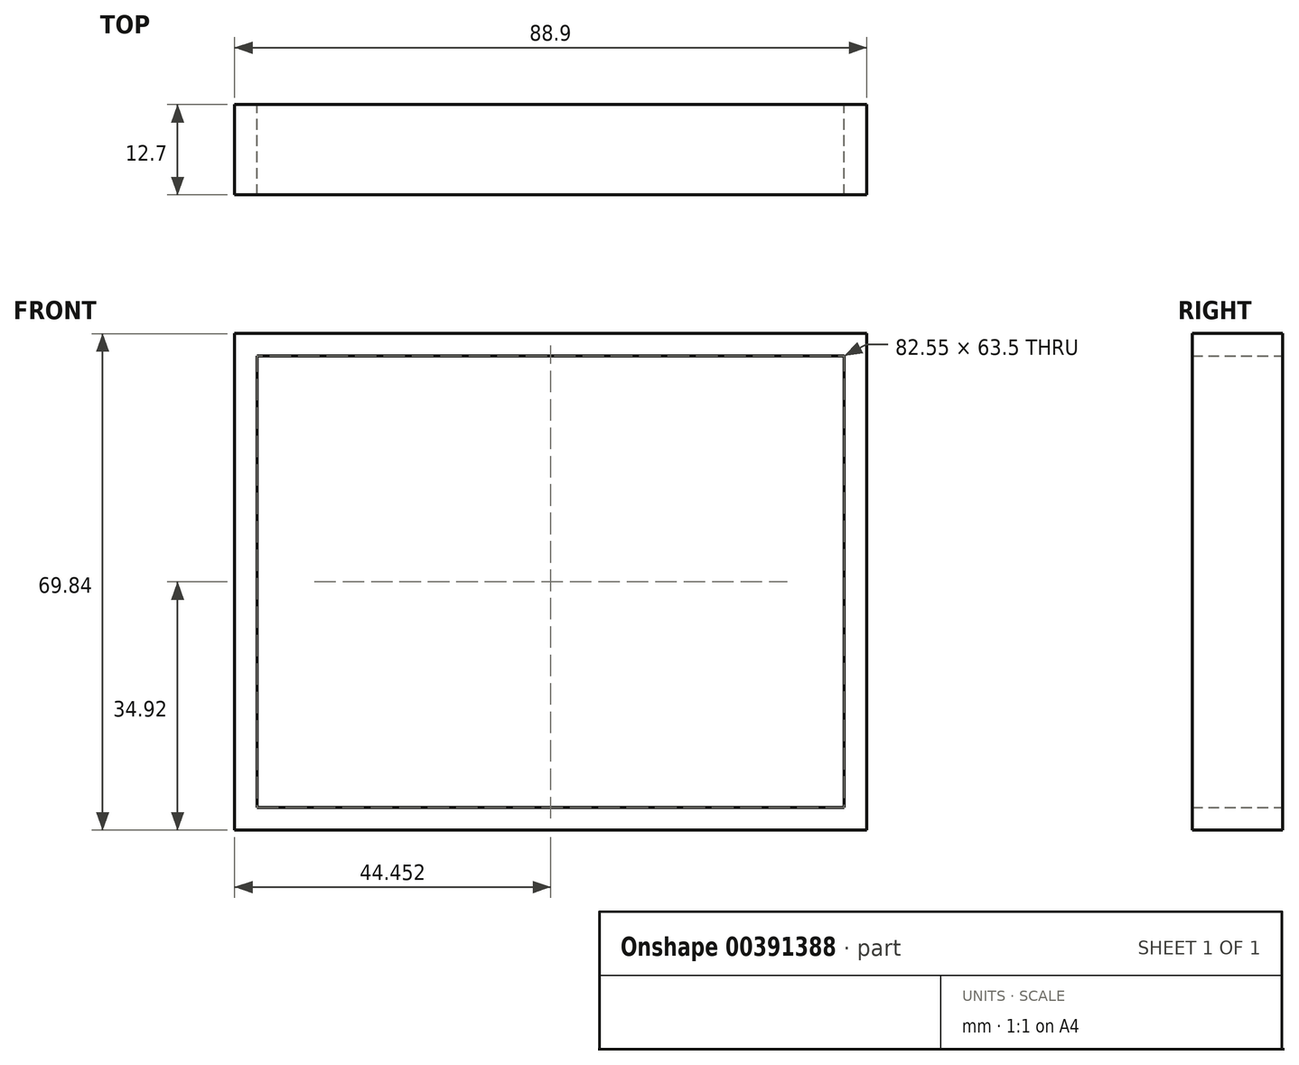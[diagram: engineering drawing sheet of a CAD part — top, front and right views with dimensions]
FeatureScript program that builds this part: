
annotation { "Feature Type Name" : "Feature", "Feature Type Description" : "" }
export const myFeature = defineFeature(function(context is Context, id is Id, definition is map)
    precondition{}
    {
        {
            var Q0;
            Q0=qCreatedBy(makeId("Front.planeOp"),FACE);
            var sketch = newSketch(context, id + "F0", { "sketchPlane" : qUnion([Q0])});
            skLineSegment(sketch, "E0.bottom", {"start": v(-0.85, 0) * mm, "end": v(81.7, 0) * mm});
            skLineSegment(sketch, "E0.top", {"start": v(-0.85, 63.5) * mm, "end": v(81.7, 63.5) * mm});
            skLineSegment(sketch, "E0.left", {"start": v(-0.85, 0) * mm, "end": v(-0.85, 63.5) * mm});
            skLineSegment(sketch, "E0.right", {"start": v(81.7, 0) * mm, "end": v(81.7, 63.5) * mm});
            skLineSegment(sketch, "E1.0", {"start": v(-4.03, 66.68) * mm, "end": v(84.87, 66.68) * mm});
            skLineSegment(sketch, "E1.1", {"start": v(-4.03, -3.17) * mm, "end": v(-4.03, 66.68) * mm});
            skLineSegment(sketch, "E1.2", {"start": v(-4.03, -3.17) * mm, "end": v(84.87, -3.17) * mm});
            skLineSegment(sketch, "E1.3", {"start": v(84.87, -3.17) * mm, "end": v(84.87, 66.68) * mm});
            skSolve(sketch);
        }
        {
            var Q0;
            Q0 = qSketchRegion(id + "F0", true);
            extrude(context, id + "F1", {"entities" : qUnion([Q0]), "depth" : 12.7 * mm});
        }
    });
